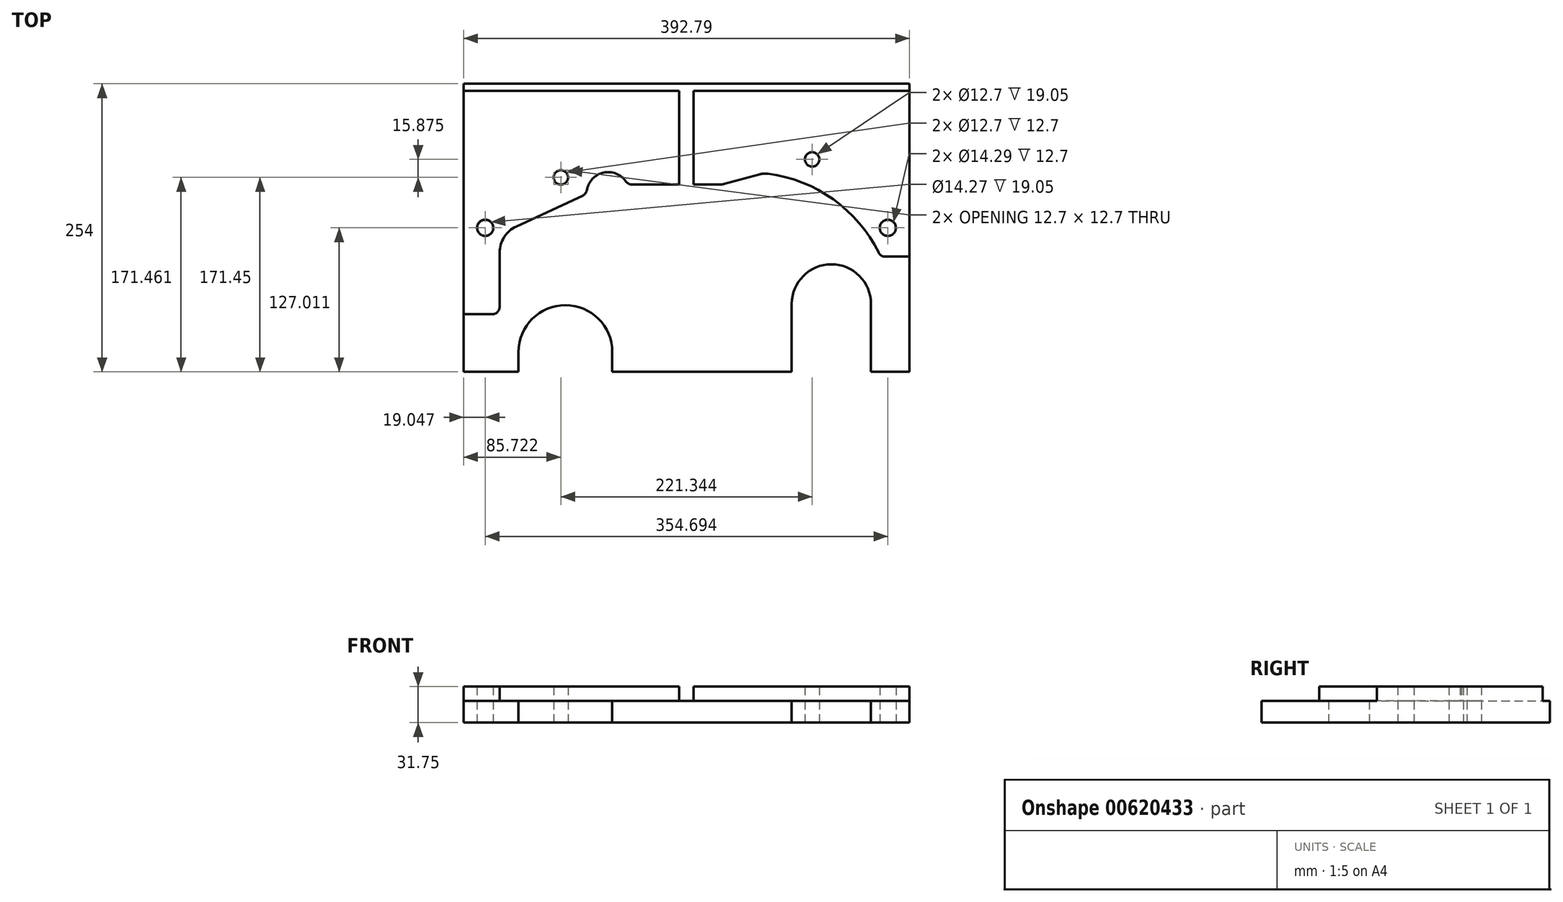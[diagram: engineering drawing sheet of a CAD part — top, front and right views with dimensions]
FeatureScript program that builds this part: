
annotation { "Feature Type Name" : "Feature", "Feature Type Description" : "" }
export const myFeature = defineFeature(function(context is Context, id is Id, definition is map)
    precondition{}
    {
        {
            var Q0;
            Q0=qCreatedBy(makeId("Top.planeOp"),FACE);
            var sketch = newSketch(context, id + "F0", { "sketchPlane" : qUnion([Q0])});
            skLineSegment(sketch, "E0", {"start": v(153.35, -127) * mm, "end": v(-112.4, -127) * mm});
            skArc(sketch, "E1", {"start": v(-112.4, -127) * mm, "mid": v(-149.75, -68.16) * mm, "end": v(-187.1, -127) * mm});
            skLineSegment(sketch, "E2", {"start": v(-187.1, -127) * mm, "end": v(-239.44, -127) * mm});
            skLineSegment(sketch, "E3", {"start": v(-239.44, -127) * mm, "end": v(-239.44, 127) * mm});
            skLineSegment(sketch, "E4", {"start": v(-239.44, 127) * mm, "end": v(153.35, 127) * mm});
            skLineSegment(sketch, "E5", {"start": v(153.35, 127) * mm, "end": v(153.35, -127) * mm});
            skCircle(sketch, "E6", {"center": v(-153.72, 44.45) * mm, "radius": 6.35 * mm});
            skCircle(sketch, "E7", {"center": v(67.63, 60.33) * mm, "radius": 6.35 * mm});
            skCircle(sketch, "E8", {"center": v(-220.4, 0) * mm, "radius": 7.14 * mm});
            skCircle(sketch, "E9", {"center": v(134.3, 0) * mm, "radius": 7.14 * mm});
            skCircle(sketch, "E10", {"center": v(84.58, -67.07) * mm, "radius": 34.93 * mm});
            skSolve(sketch);
        }
        {
            var Q0;
            Q0 = qSketchRegion(id + "F0", true);
            extrude(context, id + "F1", {"entities" : qUnion([Q0]), "depth" : 19.05 * mm, "offsetDistance" : 25.4 * mm});
        }
        {
            var Q0;
            Q0=makeQuery(id+"F1.opExtrude","CAP_FACE",FACE,{"disambiguationData":[OSD([sQuery(id+"F0.wireOp",EDGE,"E0"),sQuery(id+"F0.wireOp",EDGE,"E1"),sQuery(id+"F0.wireOp",EDGE,"E2"),sQuery(id+"F0.wireOp",EDGE,"E3"),sQuery(id+"F0.wireOp",EDGE,"E4"),sQuery(id+"F0.wireOp",EDGE,"E5"),sQuery(id+"F0.wireOp",EDGE,"E8"),sQuery(id+"F0.wireOp",EDGE,"E10"),sQuery(id+"F0.wireOp",EDGE,"E9"),sQuery(id+"F0.wireOp",EDGE,"E6"),sQuery(id+"F0.wireOp",EDGE,"E7")])],"isStart":false});
            var sketch = newSketch(context, id + "F2", { "sketchPlane" : qUnion([Q0])});
            skArc(sketch, "E11", {"start": v(-193.03, 1.2) * mm, "mid": v(-203.71, -8.17) * mm, "end": v(-207.7, -21.82) * mm});
            skArc(sketch, "E12", {"start": v(28.82, 47.68) * mm, "mid": v(25.06, 47.8) * mm, "end": v(21.36, 47.17) * mm});
            skLineSegment(sketch, "E13", {"start": v(-9.42, 38.78) * mm, "end": v(21.36, 47.17) * mm});
            skArc(sketch, "E14", {"start": v(-14.43, 38.11) * mm, "mid": v(-11.9, 38.28) * mm, "end": v(-9.42, 38.78) * mm});
            skLineSegment(sketch, "E15", {"start": v(21.36, 47.17) * mm, "end": v(-9.42, 38.78) * mm});
            skArc(sketch, "E16", {"start": v(126.32, -21.97) * mm, "mid": v(86.3, 25.08) * mm, "end": v(28.82, 47.68) * mm});
            skCircle(sketch, "E17", {"center": v(-153.72, 44.46) * mm, "radius": 6.35 * mm});
            skCircle(sketch, "E18", {"center": v(67.63, 60.34) * mm, "radius": 6.35 * mm});
            skCircle(sketch, "E19", {"center": v(-220.4, 0.01) * mm, "radius": 7.14 * mm});
            skCircle(sketch, "E20", {"center": v(134.3, 0.01) * mm, "radius": 7.14 * mm});
            skLineSegment(sketch, "E21", {"start": v(-239.44, 120.66) * mm, "end": v(-49.4, 120.66) * mm});
            skLineSegment(sketch, "E22", {"start": v(-49.4, 120.66) * mm, "end": v(-239.44, 120.66) * mm});
            skLineSegment(sketch, "E23", {"start": v(-49.4, 120.66) * mm, "end": v(-49.4, 38.11) * mm});
            skLineSegment(sketch, "E24", {"start": v(-49.4, 38.11) * mm, "end": v(-49.4, 120.66) * mm});
            skLineSegment(sketch, "E25", {"start": v(-36.7, 38.11) * mm, "end": v(-36.7, 120.66) * mm});
            skLineSegment(sketch, "E26", {"start": v(-36.7, 120.66) * mm, "end": v(-36.7, 38.11) * mm});
            skLineSegment(sketch, "E27", {"start": v(-36.7, 120.66) * mm, "end": v(153.35, 120.66) * mm});
            skLineSegment(sketch, "E28", {"start": v(153.35, 120.66) * mm, "end": v(-36.7, 120.66) * mm});
            skLineSegment(sketch, "E29", {"start": v(-49.4, 38.11) * mm, "end": v(-91.17, 38.11) * mm});
            skLineSegment(sketch, "E30", {"start": v(-91.17, 38.11) * mm, "end": v(-49.4, 38.11) * mm});
            skLineSegment(sketch, "E31", {"start": v(-239.44, -76.19) * mm, "end": v(-239.44, 120.66) * mm});
            skLineSegment(sketch, "E32", {"start": v(-214.04, -76.19) * mm, "end": v(-239.44, -76.19) * mm});
            skArc(sketch, "E33", {"start": v(-214.04, -76.19) * mm, "mid": v(-209.55, -74.33) * mm, "end": v(-207.7, -69.84) * mm});
            skLineSegment(sketch, "E34", {"start": v(-207.7, -21.82) * mm, "end": v(-207.7, -69.84) * mm});
            skArc(sketch, "E35", {"start": v(-193.03, 1.2) * mm, "mid": v(-203.72, -8.17) * mm, "end": v(-207.7, -21.82) * mm});
            skLineSegment(sketch, "E36", {"start": v(-134.46, 28.51) * mm, "end": v(-193.03, 1.2) * mm});
            skArc(sketch, "E37", {"start": v(-134.46, 28.51) * mm, "mid": v(-132.09, 30.42) * mm, "end": v(-130.88, 33.22) * mm});
            skArc(sketch, "E38", {"start": v(-96.4, 40.86) * mm, "mid": v(-116.21, 48.66) * mm, "end": v(-130.88, 33.22) * mm});
            skArc(sketch, "E39", {"start": v(-96.4, 40.86) * mm, "mid": v(-94.12, 38.84) * mm, "end": v(-91.17, 38.11) * mm});
            skLineSegment(sketch, "E40", {"start": v(-239.44, -76.19) * mm, "end": v(-214.04, -76.19) * mm});
            skLineSegment(sketch, "E41", {"start": v(131.96, -25.39) * mm, "end": v(153.35, -25.39) * mm});
            skArc(sketch, "E42", {"start": v(126.27, -21.86) * mm, "mid": v(128.6, -24.44) * mm, "end": v(131.96, -25.39) * mm});
            skArc(sketch, "E43", {"start": v(126.27, -21.86) * mm, "mid": v(86.25, 25.12) * mm, "end": v(28.82, 47.68) * mm});
            skLineSegment(sketch, "E44", {"start": v(-36.7, 38.11) * mm, "end": v(-14.43, 38.11) * mm});
            skLineSegment(sketch, "E45", {"start": v(-193.03, 1.2) * mm, "end": v(-134.46, 28.51) * mm});
            skLineSegment(sketch, "E46", {"start": v(-207.7, -69.84) * mm, "end": v(-207.7, -21.82) * mm});
            skLineSegment(sketch, "E47", {"start": v(-239.44, 120.66) * mm, "end": v(-239.44, -76.19) * mm});
            skLineSegment(sketch, "E48", {"start": v(153.35, -25.39) * mm, "end": v(153.35, 120.66) * mm});
            skLineSegment(sketch, "E49", {"start": v(-14.43, 38.11) * mm, "end": v(-36.7, 38.11) * mm});
            skLineSegment(sketch, "E50", {"start": v(153.35, -25.39) * mm, "end": v(131.96, -25.39) * mm});
            skLineSegment(sketch, "E51", {"start": v(153.35, 120.66) * mm, "end": v(153.35, -25.39) * mm});
            skSolve(sketch);
        }
        {
            var Q0;
            Q0 = qSketchRegion(id + "F2", true);
            extrude(context, id + "F3", {"entities" : qUnion([Q0]), "operationType" : NewBodyOperationType.ADD, "depth" : 12.7 * mm, "offsetDistance" : 25.4 * mm});
        }
        {
            var Q0;
            {var subQ0=sQuery(id+"F0.wireOp",EDGE,"E2");var subQ1=sQuery(id+"F0.wireOp",EDGE,"E1");var subQ2=sQuery(id+"F0.wireOp",EDGE,"E3");var subQ3=sQuery(id+"F0.wireOp",EDGE,"E0");var subQ4=sQuery(id+"F0.wireOp",EDGE,"E4");var subQ5=sQuery(id+"F0.wireOp",EDGE,"E5");var subQ6=sQuery(id+"F0.wireOp",EDGE,"E10");Q0=makeQuery(id+"F3.boolean.opBoolean","SPLIT",FACE,{"disambiguationData":[TD([makeQuery(id+"F1.opExtrude","SWEPT_FACE",FACE,{"disambiguationData":[OSD([subQ3])]})])],"derivedFrom":makeQuery(id+"F1.opExtrude","CAP_FACE",FACE,{"disambiguationData":[OSD([subQ3,subQ1,subQ0,subQ2,subQ4,subQ5,sQuery(id+"F0.wireOp",EDGE,"E8"),subQ6,sQuery(id+"F0.wireOp",EDGE,"E9"),sQuery(id+"F0.wireOp",EDGE,"E6"),sQuery(id+"F0.wireOp",EDGE,"E7")])],"isStart":false})});}
            var sketch = newSketch(context, id + "F4", { "sketchPlane" : qUnion([Q0])});
            skCircle(sketch, "E52", {"center": v(84.58, -67.07) * mm, "radius": 34.93 * mm});
            skLineSegment(sketch, "E53", {"start": v(119.5, -127) * mm, "end": v(119.5, -67.07) * mm});
            skLineSegment(sketch, "E54", {"start": v(49.65, -127) * mm, "end": v(49.65, -67.07) * mm});
            skLineSegment(sketch, "E55", {"start": v(49.65, -127) * mm, "end": v(119.5, -127) * mm});
            skSolve(sketch);
        }
        {
            var Q0;
            Q0 = qSketchRegion(id + "F4", true);
            extrude(context, id + "F5", {"entities" : qUnion([Q0]), "operationType" : NewBodyOperationType.REMOVE, "oppositeDirection" : true, "depth" : 25.4 * mm, "offsetDistance" : 25.4 * mm});
        }
        {
            var Q0;
            {var subQ0=sQuery(id+"F0.wireOp",EDGE,"E2");var subQ1=sQuery(id+"F0.wireOp",EDGE,"E1");var subQ2=sQuery(id+"F0.wireOp",EDGE,"E3");var subQ3=sQuery(id+"F0.wireOp",EDGE,"E0");var subQ4=sQuery(id+"F0.wireOp",EDGE,"E4");var subQ5=sQuery(id+"F0.wireOp",EDGE,"E5");var subQ6=sQuery(id+"F0.wireOp",EDGE,"E10");Q0=makeQuery(id+"F3.boolean.opBoolean","SPLIT",FACE,{"disambiguationData":[TD([makeQuery(id+"F1.opExtrude","SWEPT_FACE",FACE,{"disambiguationData":[OSD([subQ3])]})])],"derivedFrom":makeQuery(id+"F1.opExtrude","CAP_FACE",FACE,{"disambiguationData":[OSD([subQ3,subQ1,subQ0,subQ2,subQ4,subQ5,sQuery(id+"F0.wireOp",EDGE,"E8"),subQ6,sQuery(id+"F0.wireOp",EDGE,"E9"),sQuery(id+"F0.wireOp",EDGE,"E6"),sQuery(id+"F0.wireOp",EDGE,"E7")])],"isStart":false})});}
            var sketch = newSketch(context, id + "F6", { "sketchPlane" : qUnion([Q0])});
            skArc(sketch, "E56", {"start": v(-108.47, -109.44) * mm, "mid": v(-149.75, -68.16) * mm, "end": v(-191.02, -109.44) * mm});
            skLineSegment(sketch, "E57", {"start": v(-108.47, -127) * mm, "end": v(-108.47, -109.44) * mm});
            skLineSegment(sketch, "E58", {"start": v(-191.02, -127) * mm, "end": v(-191.02, -109.44) * mm});
            skLineSegment(sketch, "E59", {"start": v(-191.02, -127) * mm, "end": v(-108.47, -127) * mm});
            skSolve(sketch);
        }
        {
            var Q0;
            Q0 = qSketchRegion(id + "F6", true);
            extrude(context, id + "F7", {"entities" : qUnion([Q0]), "operationType" : NewBodyOperationType.REMOVE, "oppositeDirection" : true, "depth" : 25.4 * mm, "offsetDistance" : 25.4 * mm});
        }
    });
